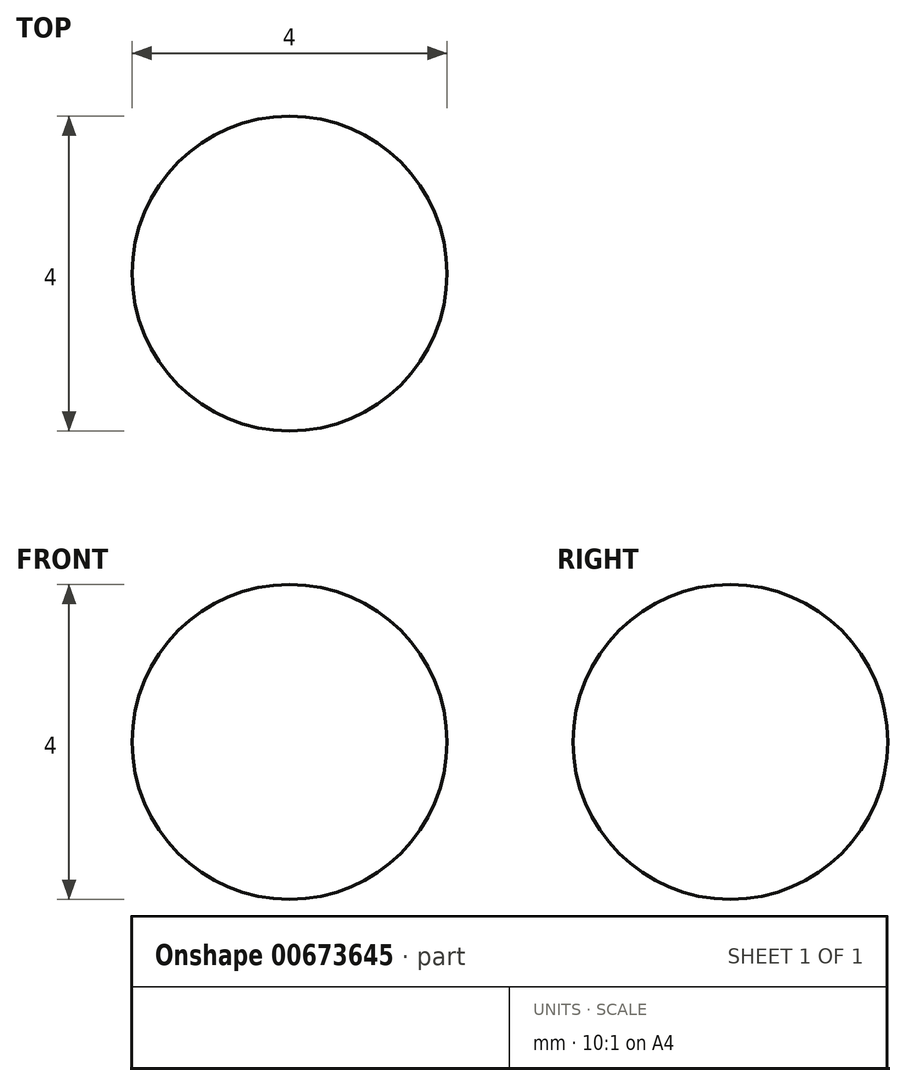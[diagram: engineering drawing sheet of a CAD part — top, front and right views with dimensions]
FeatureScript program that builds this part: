
annotation { "Feature Type Name" : "Feature", "Feature Type Description" : "" }
export const myFeature = defineFeature(function(context is Context, id is Id, definition is map)
    precondition{}
    {
        {
            var Q0;
            Q0=qCreatedBy(makeId("Front.planeOp"),FACE);
            var sketch = newSketch(context, id + "F0", { "sketchPlane" : qUnion([Q0])});
            skLineSegment(sketch, "E0", {"start": v(0, -4.76) * mm, "end": v(0, 6.47) * mm});
            skArc(sketch, "E1", {"start": v(0, 2) * mm, "mid": v(-2, 0) * mm, "end": v(0, -2) * mm});
            skSolve(sketch);
        }
        {
            var Q0;
            Q0 = qSketchRegion(id + "F0", true);
            var Q1;
            Q1=sQuery(id+"F0.wireOp",EDGE,"E0");
            revolve(context, id + "F1", {"entities" : qUnion([Q0]), "axis" : qUnion([Q1]), "revolveType" : RevolveType.FULL});
        }
    });
